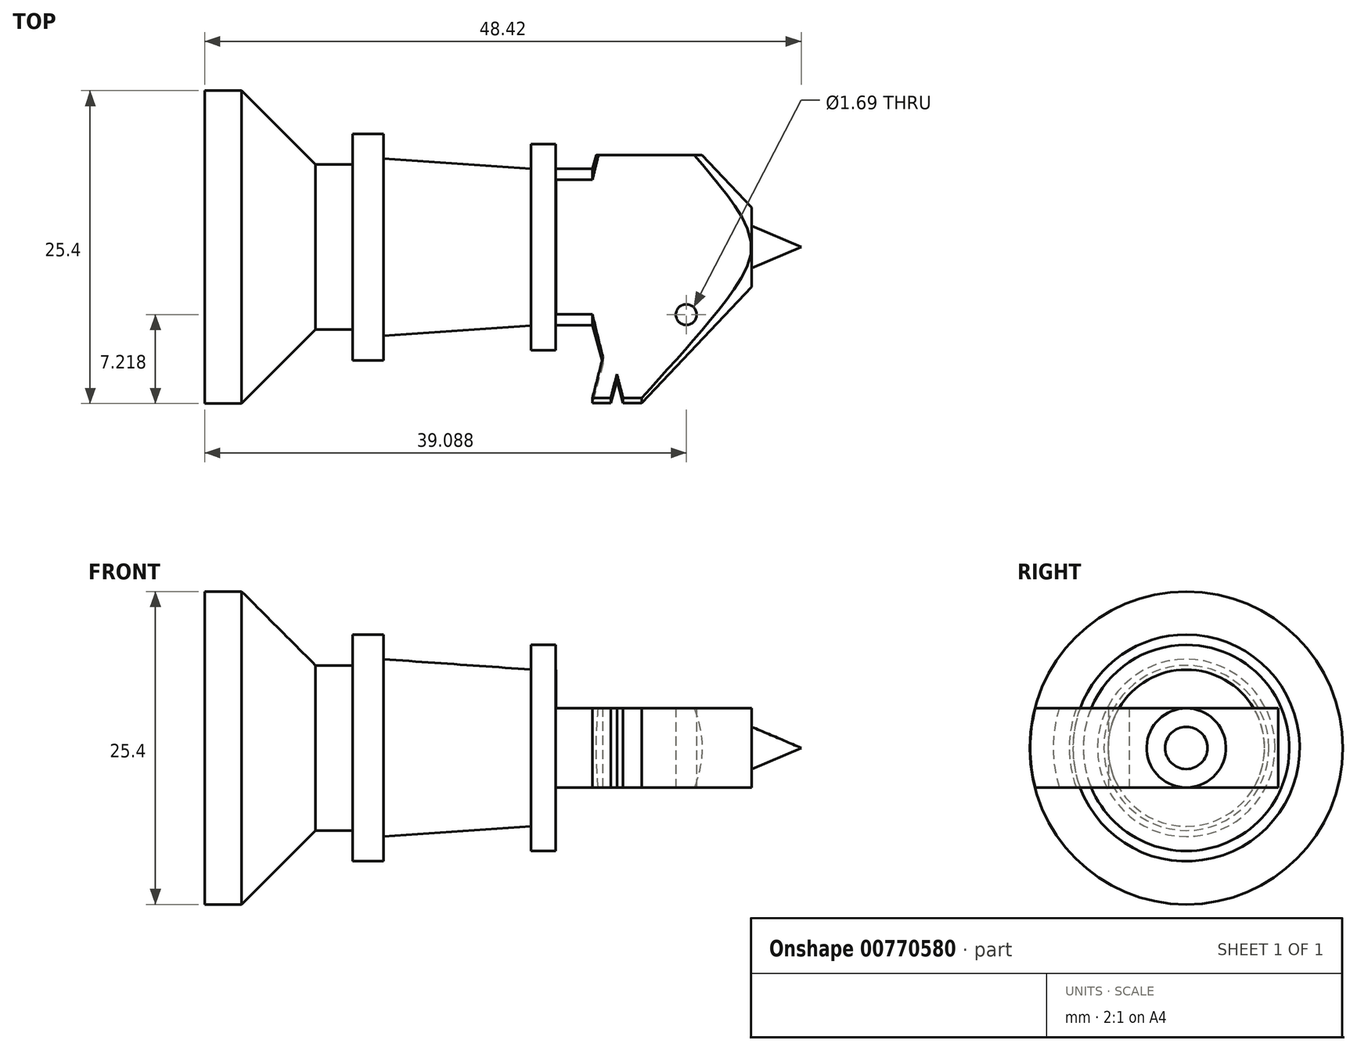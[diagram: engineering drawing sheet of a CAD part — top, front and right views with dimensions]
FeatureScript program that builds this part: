
annotation { "Feature Type Name" : "Feature", "Feature Type Description" : "" }
export const myFeature = defineFeature(function(context is Context, id is Id, definition is map)
    precondition{}
    {
        {
            var Q0;
            Q0=qCreatedBy(makeId("Front.planeOp"),FACE);
            var sketch = newSketch(context, id + "F0", { "sketchPlane" : qUnion([Q0])});
            skLineSegment(sketch, "E0", {"start": v(-24.97, 0) * mm, "end": v(23.45, 0) * mm});
            skLineSegment(sketch, "E1", {"start": v(-24.97, 0) * mm, "end": v(-24.97, 12.7) * mm});
            skLineSegment(sketch, "E2", {"start": v(-24.97, 12.7) * mm, "end": v(-21.97, 12.7) * mm});
            skLineSegment(sketch, "E3", {"start": v(-21.97, 12.7) * mm, "end": v(-15.97, 6.7) * mm});
            skLineSegment(sketch, "E4", {"start": v(-15.97, 6.7) * mm, "end": v(-12.97, 6.7) * mm});
            skLineSegment(sketch, "E5", {"start": v(-12.97, 6.7) * mm, "end": v(-12.97, 9.2) * mm});
            skLineSegment(sketch, "E6", {"start": v(-12.97, 9.2) * mm, "end": v(-10.47, 9.2) * mm});
            skLineSegment(sketch, "E7", {"start": v(-10.47, 9.2) * mm, "end": v(-10.47, 7.2) * mm});
            skLineSegment(sketch, "E8", {"start": v(-10.47, 7.2) * mm, "end": v(1.5, 6.36) * mm});
            skLineSegment(sketch, "E9", {"start": v(1.5, 6.36) * mm, "end": v(1.5, 8.36) * mm});
            skLineSegment(sketch, "E10", {"start": v(1.5, 8.36) * mm, "end": v(3.5, 8.36) * mm});
            skLineSegment(sketch, "E11", {"start": v(3.5, 8.36) * mm, "end": v(3.5, 6.35) * mm});
            skLineSegment(sketch, "E12", {"start": v(3.5, 6.35) * mm, "end": v(6.5, 6.35) * mm});
            skLineSegment(sketch, "E13", {"start": v(6.5, 6.35) * mm, "end": v(7.35, 9.5) * mm});
            skLineSegment(sketch, "E14", {"start": v(7.35, 9.5) * mm, "end": v(6.5, 12.67) * mm});
            skLineSegment(sketch, "E15", {"start": v(6.5, 12.67) * mm, "end": v(7.99, 12.67) * mm});
            skLineSegment(sketch, "E16", {"start": v(7.99, 12.67) * mm, "end": v(8.49, 10.8) * mm});
            skLineSegment(sketch, "E17", {"start": v(8.49, 10.8) * mm, "end": v(8.99, 12.67) * mm});
            skLineSegment(sketch, "E18.trimOffspring", {"start": v(8.99, 12.67) * mm, "end": v(10.49, 12.67) * mm});
            skLineSegment(sketch, "E19", {"start": v(10.49, 12.67) * mm, "end": v(19.41, 3.22) * mm});
            skLineSegment(sketch, "E20", {"start": v(19.41, 3.22) * mm, "end": v(19.41, 1.72) * mm});
            skLineSegment(sketch, "E21", {"start": v(23.45, 0) * mm, "end": v(19.41, 1.72) * mm});
            skSolve(sketch);
        }
        {
            var Q0;
            Q0 = qSketchRegion(id + "F0", true);
            var Q1;
            Q1=sQuery(id+"F0.wireOp",EDGE,"E0");
            revolve(context, id + "F1", {"surfaceOperationType" : NewSurfaceOperationType.NEW, "entities" : qUnion([Q0]), "axis" : qUnion([Q1]), "revolveType" : RevolveType.FULL});
        }
        {
            var Q0;
            Q0=qCreatedBy(makeId("Front.planeOp"),FACE);
            var sketch = newSketch(context, id + "F2", { "sketchPlane" : qUnion([Q0])});
            skLineSegment(sketch, "E22", {"start": v(19.7, 3.23) * mm, "end": v(3.55, 3.23) * mm});
            skLineSegment(sketch, "E23", {"start": v(3.55, 3.23) * mm, "end": v(3.55, 36.56) * mm});
            skLineSegment(sketch, "E24", {"start": v(3.55, 36.56) * mm, "end": v(19.7, 36.56) * mm});
            skLineSegment(sketch, "E25", {"start": v(19.7, 36.56) * mm, "end": v(19.7, 3.23) * mm});
            skSolve(sketch);
        }
        {
            var Q0;
            Q0=makeQuery(id+"F2.imprint","IMPRINT",FACE,{"disambiguationData":[TD([[makeQuery(id+"F2.imprint","IMPRINT",EDGE,{"derivedFrom":sQuery(id+"F2.wireOp",EDGE,"E22")}),-1.0]])]});
            extrude(context, id + "F3", {"entities" : qUnion([Q0]), "operationType" : NewBodyOperationType.REMOVE, "oppositeDirection" : true, "depth" : 25 * mm, "offsetDistance" : 25 * mm});
        }
        {
            var Q0;
            Q0=makeQuery(id+"F2.imprint","IMPRINT",FACE,{"disambiguationData":[TD([[makeQuery(id+"F2.imprint","IMPRINT",EDGE,{"derivedFrom":sQuery(id+"F2.wireOp",EDGE,"E22")}),-1.0]])]});
            extrude(context, id + "F4", {"entities" : qUnion([Q0]), "operationType" : NewBodyOperationType.REMOVE, "depth" : 25 * mm, "offsetDistance" : 25 * mm});
        }
        {
            var Q0;
            Q0=qCreatedBy(makeId("Front.planeOp"),FACE);
            var sketch = newSketch(context, id + "F5", { "sketchPlane" : qUnion([Q0])});
            skLineSegment(sketch, "E26", {"start": v(19.44, -3.2) * mm, "end": v(3.5, -3.2) * mm});
            skLineSegment(sketch, "E27", {"start": v(3.5, -3.2) * mm, "end": v(3.5, -22.65) * mm});
            skLineSegment(sketch, "E28", {"start": v(3.5, -22.65) * mm, "end": v(19.44, -22.65) * mm});
            skLineSegment(sketch, "E29", {"start": v(19.44, -22.65) * mm, "end": v(19.44, -3.2) * mm});
            skSolve(sketch);
        }
        {
            var Q0;
            Q0 = qSketchRegion(id + "F5", true);
            extrude(context, id + "F6", {"entities" : qUnion([Q0]), "operationType" : NewBodyOperationType.REMOVE, "oppositeDirection" : true, "depth" : 50 * mm, "offsetDistance" : 25 * mm});
        }
        {
            var Q0;
            Q0=makeQuery(id+"F5.imprint","IMPRINT",FACE,{"disambiguationData":[TD([[makeQuery(id+"F5.imprint","IMPRINT",EDGE,{"derivedFrom":sQuery(id+"F5.wireOp",EDGE,"E26")}),1.0]])]});
            extrude(context, id + "F7", {"entities" : qUnion([Q0]), "operationType" : NewBodyOperationType.REMOVE, "endBound" : BoundingType.THROUGH_ALL, "depth" : 25 * mm, "offsetDistance" : 25 * mm});
        }
        {
            var Q0;
            {var subQ0=sQuery(id+"F2.wireOp",EDGE,"E22");Q0=makeQuery(id+"F4.boolean.opBoolean","MERGE",FACE,{"derivedFrom":[makeQuery(id+"F3.boolean.opBoolean","COPY",FACE,{"derivedFrom":makeQuery(id+"F3.opExtrude","SWEPT_FACE",FACE,{"disambiguationData":[OSD([subQ0])]})}),makeQuery(id+"F4.opExtrude","SWEPT_FACE",FACE,{"disambiguationData":[OSD([subQ0])]})]});}
            var sketch = newSketch(context, id + "F8", { "sketchPlane" : qUnion([Q0])});
            skLineSegment(sketch, "E30", {"start": v(19.19, 7.47) * mm, "end": v(19.19, 19.49) * mm});
            skLineSegment(sketch, "E31", {"start": v(19.19, 19.49) * mm, "end": v(5.36, 19.49) * mm});
            skLineSegment(sketch, "E32", {"start": v(5.36, 19.49) * mm, "end": v(5.36, 7.47) * mm});
            skLineSegment(sketch, "E33", {"start": v(5.36, 7.47) * mm, "end": v(19.19, 7.47) * mm});
            skSolve(sketch);
        }
        {
            var Q0;
            Q0 = qSketchRegion(id + "F8", true);
            extrude(context, id + "F9", {"entities" : qUnion([Q0]), "operationType" : NewBodyOperationType.REMOVE, "oppositeDirection" : true, "depth" : 50 * mm, "offsetDistance" : 25 * mm});
        }
        {
            var Q0;
            {var subQ0=sQuery(id+"F5.wireOp",EDGE,"E26");Q0=makeQuery(id+"F7.boolean.opBoolean","MERGE",FACE,{"derivedFrom":[makeQuery(id+"F6.boolean.opBoolean","COPY",FACE,{"derivedFrom":makeQuery(id+"F6.opExtrude","SWEPT_FACE",FACE,{"disambiguationData":[OSD([subQ0])]})}),makeQuery(id+"F7.opExtrude","SWEPT_FACE",FACE,{"disambiguationData":[OSD([subQ0])]})]});}
            var sketch = newSketch(context, id + "F10", { "sketchPlane" : qUnion([Q0])});
            skCircle(sketch, "E34", {"center": v(14.12, 5.48) * mm, "radius": 0.84 * mm});
            skSolve(sketch);
        }
        {
            var Q0;
            Q0 = qSketchRegion(id + "F10", true);
            extrude(context, id + "F11", {"entities" : qUnion([Q0]), "operationType" : NewBodyOperationType.REMOVE, "oppositeDirection" : true, "depth" : 50 * mm, "offsetDistance" : 25 * mm});
        }
    });
